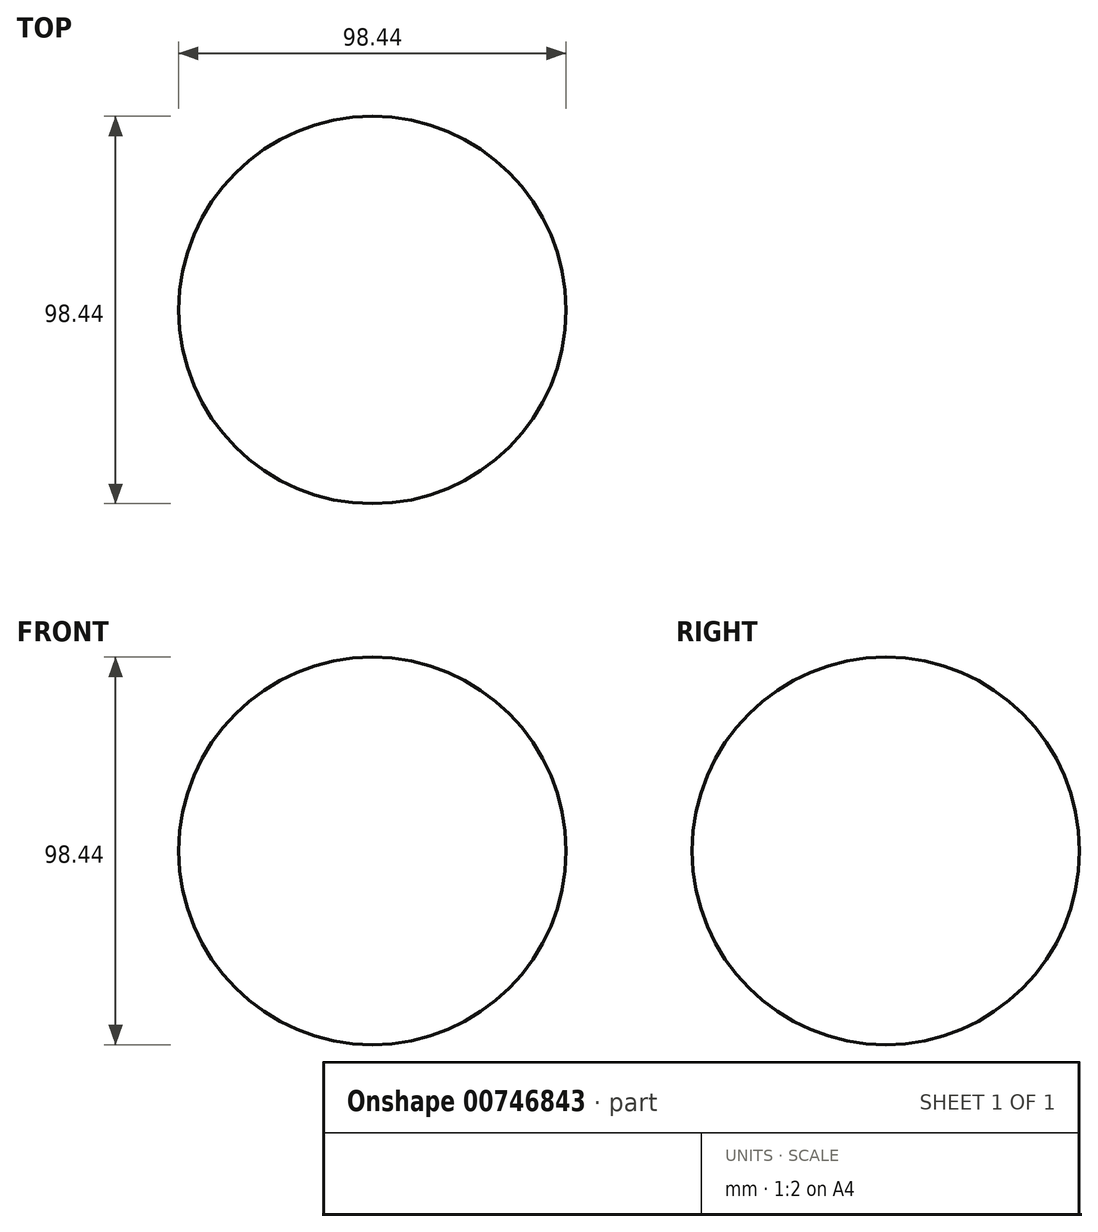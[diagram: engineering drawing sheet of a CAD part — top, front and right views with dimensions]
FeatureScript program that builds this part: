
annotation { "Feature Type Name" : "Feature", "Feature Type Description" : "" }
export const myFeature = defineFeature(function(context is Context, id is Id, definition is map)
    precondition{}
    {
        {
            var Q0;
            Q0=qCreatedBy(makeId("Front.planeOp"),FACE);
            var sketch = newSketch(context, id + "F0", { "sketchPlane" : qUnion([Q0])});
            skArc(sketch, "E0", {"start": v(0, -49.22) * mm, "mid": v(49.22, 0) * mm, "end": v(0, 49.22) * mm});
            skLineSegment(sketch, "E1", {"start": v(0, 49.22) * mm, "end": v(0, -49.22) * mm});
            skSolve(sketch);
        }
        {
            var Q0;
            Q0=makeQuery(id+"F0.imprint","IMPRINT",FACE,{"disambiguationData":[TD([[makeQuery(id+"F0.imprint","IMPRINT",EDGE,{"derivedFrom":sQuery(id+"F0.wireOp",EDGE,"E0")}),1.0]])]});
            var Q1;
            Q1=sQuery(id+"F0.wireOp",EDGE,"E1");
            revolve(context, id + "F1", {"surfaceOperationType" : NewSurfaceOperationType.NEW, "entities" : qUnion([Q0]), "axis" : qUnion([Q1]), "revolveType" : RevolveType.FULL});
        }
    });
